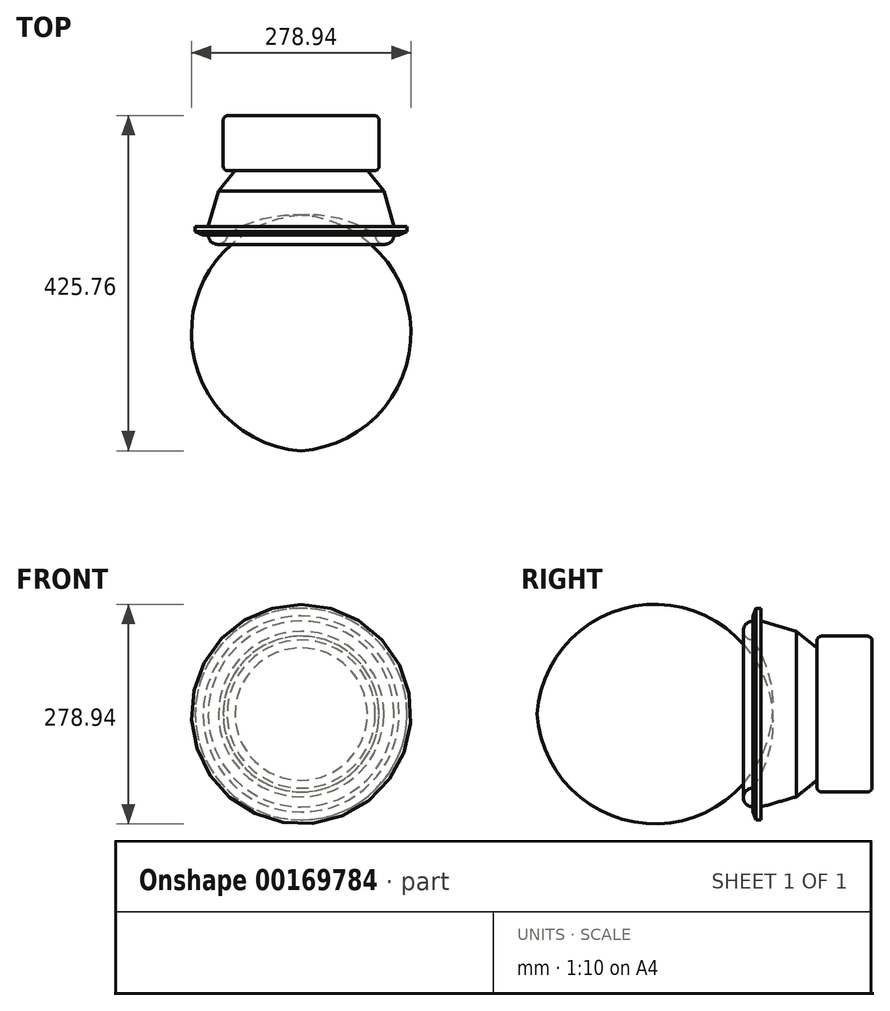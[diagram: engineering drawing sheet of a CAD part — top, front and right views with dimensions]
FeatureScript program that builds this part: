
annotation { "Feature Type Name" : "Feature", "Feature Type Description" : "" }
export const myFeature = defineFeature(function(context is Context, id is Id, definition is map)
    precondition{}
    {
        {
            var Q0;
            Q0=qCreatedBy(makeId("Right.planeOp"),FACE);
            var sketch = newSketch(context, id + "F0", { "sketchPlane" : qUnion([Q0])});
            skLineSegment(sketch, "E0", {"start": v(14.5, 0) * mm, "end": v(141, 0) * mm});
            skLineSegment(sketch, "E1", {"start": v(141, 0) * mm, "end": v(141, 99) * mm});
            skLineSegment(sketch, "E2", {"start": v(141, 99) * mm, "end": v(71, 99) * mm});
            skLineSegment(sketch, "E3", {"start": v(71, 99) * mm, "end": v(71, 84) * mm});
            skLineSegment(sketch, "E4", {"start": v(0, 118) * mm, "end": v(0, 134.5) * mm});
            skLineSegment(sketch, "E5", {"start": v(0, 134.5) * mm, "end": v(-10.5, 134.5) * mm});
            skLineSegment(sketch, "E6", {"start": v(-10.5, 134.5) * mm, "end": v(-10.5, 118) * mm});
            skArc(sketch, "E7", {"start": v(-10.5, 118) * mm, "mid": v(-22.5, 106) * mm, "end": v(-10.5, 94) * mm});
            skLineSegment(sketch, "E8", {"start": v(0, 118) * mm, "end": v(45, 105) * mm});
            skLineSegment(sketch, "E9", {"start": v(45, 105) * mm, "end": v(71, 84) * mm});
            skLineSegment(sketch, "E10", {"start": v(-81.69, 0) * mm, "end": v(-10.5, 0) * mm, "construction": true});
            skArc(sketch, "E11", {"start": v(14.5, 0) * mm, "mid": v(9.83, 49.08) * mm, "end": v(-10.5, 94) * mm});
            skLineSegment(sketch, "E12.trimOffspring", {"start": v(14.5, 0) * mm, "end": v(179.7, 0) * mm, "construction": true});
            skPoint(sketch, "E13.end.orphan", {"position": v(0, 0) * mm});
            skSolve(sketch);
        }
        {
            var Q0;
            Q0=makeQuery(id+"F0.imprint","IMPRINT",FACE,{"disambiguationData":[TD([[makeQuery(id+"F0.imprint","IMPRINT",EDGE,{"derivedFrom":sQuery(id+"F0.wireOp",EDGE,"E0")}),1.0]])]});
            var Q1;
            Q1=sQuery(id+"F0.wireOp",EDGE,"E10");
            revolve(context, id + "F1", {"entities" : qUnion([Q0]), "axis" : qUnion([Q1]), "revolveType" : RevolveType.FULL});
        }
        {
            var Q0;
            Q0=makeQuery(id+"F1.opRevolve","SWEPT_EDGE",EDGE,{"disambiguationData":[OSD([sQuery(id+"F0.wireOp",EDGE,"E5"),sQuery(id+"F0.wireOp",EDGE,"E6")])]});
            chamfer(context, id + "F2", {"entities" : qUnion([Q0]), "chamferType" : ChamferType.TWO_OFFSETS, "width1" : 10 * mm, "oppositeDirection" : false, "width2" : 4 * mm, "tangentPropagation" : true});
        }
        {
            var Q0;
            Q0=makeQuery(id+"F1.opRevolve","SWEPT_FACE",FACE,{"disambiguationData":[OSD([sQuery(id+"F0.wireOp",EDGE,"E2")])]});
            fillet(context, id + "F3", {"entities" : qUnion([Q0]), "radius" : 6 * mm, "tangentPropagation" : true, "allowEdgeOverflow" : false});
        }
    });
